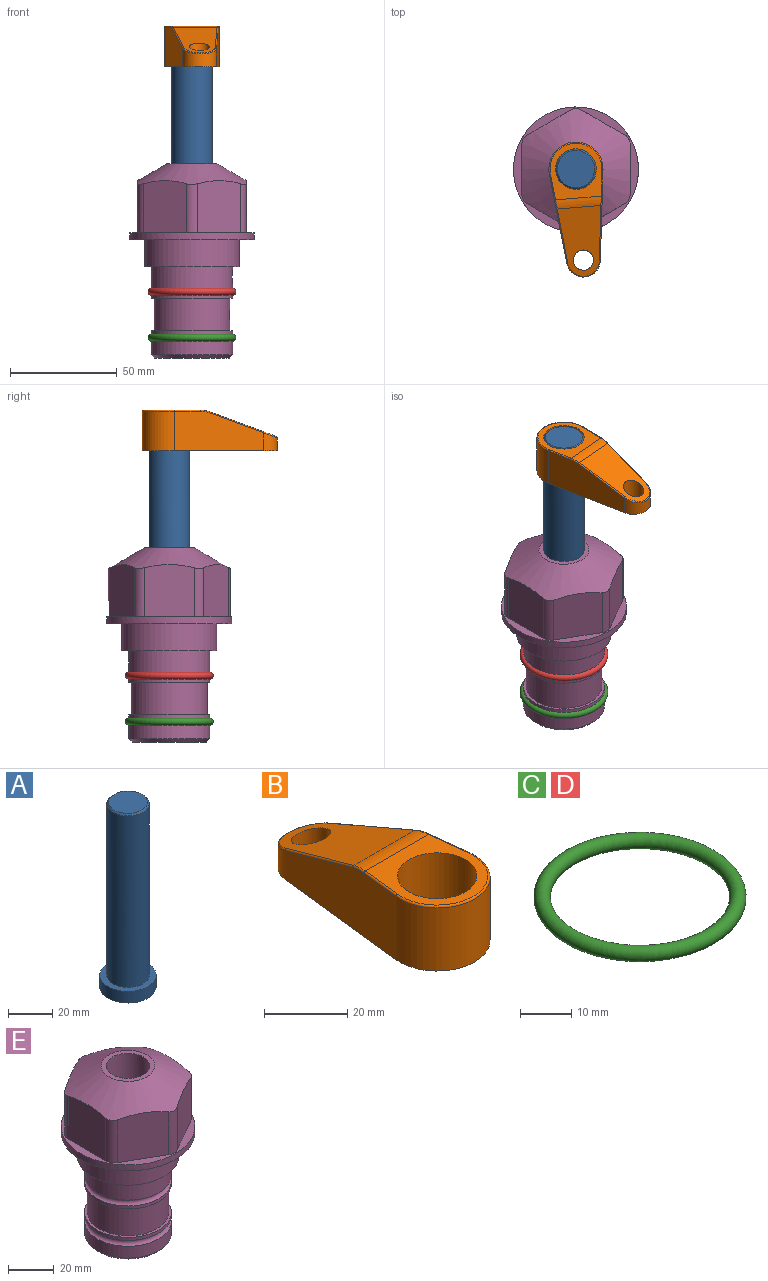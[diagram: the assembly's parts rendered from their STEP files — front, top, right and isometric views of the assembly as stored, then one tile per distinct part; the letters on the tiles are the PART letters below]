
ASSEMBLY  parts=5 mates=3
PART A: 6 faces, bbox 25.4x25.4x101.6 mm
  f0: plane 17.46x17.46mm, normal (0,0,1), area 239.5mm2, adj f5
  f1: plane 25.4x25.4mm, normal (0,0,-1), area 506.7mm2, adj f2
  f2: cylinder r=12.7mm len=25.4mm, axis (0,0,1), area 506.7mm2, adj f1,f3
  f3: plane 25.4x25.4mm, normal (0,0,1), area 221.7mm2, adj f2,f4
  f4: cylinder r=9.53mm len=94.46mm, axis (0,0,1), area 5653mm2, adj f3,f5
  f5: cone r=8.73mm half-angle=45deg, axis (0,0,-1), area 64.4mm2, adj f0,f4
PART B: 44 faces, bbox 27.5x64.5x19.1 mm
  f0: plane 2.3x0.95mm, normal (0,0,-1), area 1mm2, adj f25,f30,f34
  f1: plane 63.5x25.4mm, normal (0,0,-1), area 561.7mm2, adj f2,f3,f4,f5,f6,f7,f19,f20
  f2: cylinder r=12.7mm len=25.4mm, axis (0,0,-1), area 792.2mm2, adj f1,f3,f5,f13
  f3: plane 42.33x18.54mm, normal (0.99,0.11,0), area 647mm2, adj f1,f2,f4,f11,f12,f14
  f4: cylinder r=7.94mm len=15.78mm, axis (0,0,-1), area 158.6mm2, adj f1,f3,f5,f16
  f5: plane 42.33x18.54mm, normal (-0.99,0.11,0), area 647mm2, adj f1,f2,f4,f15,f17,f18
  f6: cylinder r=9.53mm len=19.05mm, axis (0,0,-1), area 1140.1mm2, adj f1,f8
  f7: cylinder r=4.76mm len=10.98mm, axis (0,0,-1), area 276.1mm2, adj f1,f9
  f8: plane 25.83x24.38mm, normal (0,0,1), area 262.2mm2, adj f6,f10,f11,f13,f15
  f9: plane 32.49x20.55mm, normal (0,0.34,0.94), area 489.9mm2, adj f7,f10,f14,f16,f18
  f10: cylinder r=12.7mm len=21.49mm, axis (-1,0,0), area 93.2mm2, adj f8,f9,f12,f17
  f11: cylinder r=0.51mm len=12.34mm, axis (0.11,-0.99,0), area 9.9mm2, adj f3,f8,f12,f13
  f12: bspline ~7.62x1.64mm, area 3.5mm2, adj f3,f10,f11,f14
  f13: torus R=12.19mm, axis (0,0,1), area 33.6mm2, adj f2,f8,f11,f15
  f14: cylinder r=0.51mm len=26.01mm, axis (0.1,-0.93,0.34), area 21.6mm2, adj f3,f9,f12,f16
  f15: cylinder r=0.51mm len=12.34mm, axis (0.11,0.99,0), area 9.9mm2, adj f5,f8,f13,f17
  f16: bspline ~15.78x7.05mm, area 15.7mm2, adj f4,f9,f14,f18
  f17: bspline ~7.62x1.64mm, area 3.5mm2, adj f5,f10,f15,f18
  f18: cylinder r=0.51mm len=26.01mm, axis (0.1,0.93,-0.34), area 21.6mm2, adj f5,f9,f16,f17
  f19: plane 21.6x14.29mm, normal (-0.99,-0.11,0), area 242.6mm2, adj f1,f26,f28,f34,f36,f38
  f20: plane 21.6x14.29mm, normal (0.99,-0.11,0), area 242.6mm2, adj f1,f27,f29,f37,f39,f41
  f21: cylinder r=12.7mm len=14.29mm, axis (0,0,-1), area 173.2mm2, adj f1,f26,f27,f30,f31,f33
  f22: cylinder r=7.94mm len=7.63mm, axis (0,0,-1), area 53.8mm2, adj f1,f28,f29,f42
  f23: plane 2.3x0.95mm, normal (0,0,-1), area 1mm2, adj f25,f33,f37
  f24: plane 17.94x12.32mm, normal (0,-0.34,-0.94), area 191.2mm2, adj f25,f38,f41,f42
  f25: cylinder r=9.53mm len=12.93mm, axis (-1,0,0), area 37.5mm2, adj f0,f23,f24,f31,f36,f39
  f26: cylinder r=1.59mm len=14.29mm, axis (0,0,-1), area 49mm2, adj f1,f19,f21,f32
  f27: cylinder r=1.59mm len=14.29mm, axis (0,0,-1), area 49mm2, adj f1,f20,f21,f35
  f28: cylinder r=1.59mm len=7.28mm, axis (0,0,-1), area 22.1mm2, adj f1,f19,f22,f40
  f29: cylinder r=1.59mm len=7.28mm, axis (0,0,-1), area 22.1mm2, adj f1,f20,f22,f43
  f30: torus R=14.29mm, axis (0,0,1), area 5.8mm2, adj f0,f21,f31,f32
  f31: bspline ~11.06x2.73mm, area 20.8mm2, adj f21,f25,f30,f33
  f32: sphere r=1.59mm, area 5.4mm2, adj f26,f30,f34
  f33: torus R=14.29mm, axis (0,0,1), area 5.8mm2, adj f21,f23,f31,f35
  f34: cylinder r=1.59mm len=1.68mm, axis (-0.11,0.99,0), area 2.4mm2, adj f0,f19,f32,f36
  f35: sphere r=1.59mm, area 5.4mm2, adj f27,f33,f37
  f36: bspline ~5.82x2.33mm, area 7.7mm2, adj f19,f25,f34,f38
  f37: cylinder r=1.59mm len=1.68mm, axis (0.11,0.99,0), area 2.4mm2, adj f20,f23,f35,f39
  f38: cylinder r=1.59mm len=18.33mm, axis (0.1,-0.93,0.34), area 46.7mm2, adj f19,f24,f36,f40
  f39: bspline ~5.82x2.33mm, area 7.7mm2, adj f20,f25,f37,f41
  f40: sphere r=1.59mm, area 3.6mm2, adj f28,f38,f42
  f41: cylinder r=1.59mm len=18.33mm, axis (0.1,0.93,-0.34), area 46.7mm2, adj f20,f24,f39,f43
  f42: bspline ~8.31x1.84mm, area 15.3mm2, adj f22,f24,f40,f43
  f43: sphere r=1.59mm, area 3.6mm2, adj f29,f41,f42
PART C: 1 faces, bbox 44.7x44.7x3.2 mm
  f0: torus R=19.05mm, axis (0,0,1), area 1193.9mm2
PART D: same geometry as C
PART E: 36 faces, bbox 58.7x58.7x91.2 mm
  f0: cylinder r=17.78mm len=35.56mm, axis (0,0,1), area 1670.8mm2, adj f23,f24,f31
  f1: cylinder r=19.05mm len=38.1mm, axis (0,0,1), area 1191.9mm2, adj f26,f27,f30
  f2: plane 58.66x58.66mm, normal (0,0,-1), area 1150.6mm2, adj f3,f28
  f3: cylinder r=29.33mm len=58.66mm, axis (0,0,-1), area 585.1mm2, adj f2,f4
  f4: plane 58.66x58.66mm, normal (0,0,1), area 475.9mm2, adj f3,f5,f6,f7,f8,f9,f10,f11
  f5: plane 24.5x20.32mm, normal (-0.5,0.87,0), area 562.8mm2, adj f4,f15,f16,f17
  f6: plane 24.5x20.32mm, normal (0.5,0.87,0), area 562.8mm2, adj f4,f14,f15,f17
  f7: plane 24.5x23.48mm, normal (1,0,0), area 562.8mm2, adj f4,f13,f14,f17
  f8: plane 24.5x20.32mm, normal (0.5,-0.87,0), area 562.8mm2, adj f4,f12,f13,f17
  f9: plane 24.5x20.32mm, normal (-0.5,-0.87,0), area 562.8mm2, adj f4,f11,f12,f17
  f10: plane 24.5x23.48mm, normal (-1,0,0), area 562.8mm2, adj f4,f11,f16,f17
  f11: cylinder r=5.08mm len=23.01mm, axis (0,0,-1), area 121.2mm2, adj f4,f9,f10,f17
  f12: cylinder r=5.08mm len=23.01mm, axis (0,0,-1), area 121.2mm2, adj f4,f8,f9,f17
  f13: cylinder r=5.08mm len=23.01mm, axis (0,0,-1), area 121.2mm2, adj f4,f7,f8,f17
  f14: cylinder r=5.08mm len=23.01mm, axis (0,0,-1), area 121.2mm2, adj f4,f6,f7,f17
  f15: cylinder r=5.08mm len=23.01mm, axis (0,0,-1), area 121.2mm2, adj f4,f5,f6,f17
  f16: cylinder r=5.08mm len=23.01mm, axis (0,0,-1), area 121.2mm2, adj f4,f5,f10,f17
  f17: cone r=11.73mm half-angle=60deg, axis (0,0,-1), area 2071.8mm2, adj f5,f6,f7,f8,f9,f10,f11,f12
  f18: plane 23.46x23.46mm, normal (0,0,1), area 147.4mm2, adj f17,f35
  f19: plane 34.93x34.93mm, normal (0,0,-1), area 958mm2, adj f29
  f20: cylinder r=19.05mm len=38.1mm, axis (0,0,1), area 760.1mm2, adj f21,f29
  f21: torus R=19.05mm, axis (0,0,1), area 565.3mm2, adj f20,f22
  f22: cylinder r=19.05mm len=38.1mm, axis (0,0,1), area 190mm2, adj f21,f23
  f23: plane 38.1x38.1mm, normal (0,0,1), area 146.9mm2, adj f0,f22
  f24: plane 38.1x38.1mm, normal (0,0,-1), area 146.9mm2, adj f0,f25
  f25: cylinder r=19.05mm len=38.1mm, axis (0,0,1), area 190mm2, adj f24,f26
  f26: torus R=19.05mm, axis (0,0,1), area 565.3mm2, adj f1,f25
  f27: plane 44.45x44.45mm, normal (0,0,-1), area 411.7mm2, adj f1,f28
  f28: cylinder r=22.23mm len=44.45mm, axis (0,0,1), area 1773.5mm2, adj f2,f27
  f29: cone r=19.05mm half-angle=45deg, axis (0,0,1), area 257.5mm2, adj f19,f20
  f30: cylinder r=3.17mm len=6.75mm, axis (-1,0,0), area 128mm2, adj f1,f33
  f31: cylinder r=3.17mm len=6.35mm, axis (-1,0,0), area 102.5mm2, adj f0,f33
  f32: plane 25.4x25.4mm, normal (0,0,1), area 506.7mm2, adj f33
  f33: cylinder r=12.7mm len=66.42mm, axis (0,0,-1), area 5236.2mm2, adj f30,f31,f32,f34
  f34: cone r=9.53mm half-angle=30deg, axis (0,0,-1), area 443.4mm2, adj f33,f35
  f35: cylinder r=9.53mm len=19.05mm, axis (0,0,-1), area 849mm2, adj f18,f34
PLACE A rot(axis=(0,0,-1),85.3deg) t=(0,0,26.58)mm
PLACE B rot(axis=(0,0,-1),175.3deg) t=(0,0,81.19)mm
PLACE C t=(0,0,-21.59)mm
PLACE D at identity
PLACE E at identity fixed
MATE fastened C.f0 <-> E.f0  axis (0,0,1) through (0,0,-46.1)mm
MATE cylindrical A.f2 <-> E.f0  axis (0,0,1) through (0,0,52.22)mm
MATE fastened B.f2 <-> A.f2  axis (0,0,1) through (0,0,100.24)mm
